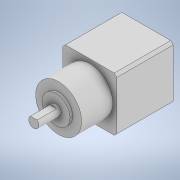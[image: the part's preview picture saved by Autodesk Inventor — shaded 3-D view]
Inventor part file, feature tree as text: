
AUTODESK INVENTOR PART (.ipt)
format: ipt  version: 2021 (Build 250183000, 183)  size: 137,216 bytes
history: native  units: mm
features: extrude x5, sketch x4
ambient origin geometry x8: Origin, YZ Plane, XZ Plane, XY Plane, X Axis, Y Axis, Z Axis, Center Point
bodies: Solid1 (feature_tree)
feature tree (9):
  extrude  "Extrusion1"  Depth=2.0mm
  extrude  "Extrusion2"  Depth=2.0mm
  extrude  "Extrusion3"  Depth=2.0mm
  sketch  "Sketch4"  dims[d6=2.0mm d7=2.0mm d8=42.3mm d9=42.3mm d10=44.2mm d11=0.0mm d12=36.0mm d13=24.5mm d14=0.0mm d15=22.0mm d16=2.0mm d17=0.0mm d18=8.0mm d19=7.0mm d20=17.5mm d21=0.0mm d22=2.3mm d23=0.0mm]
  extrude  "Extrusion4"  Depth=2.0mm
  extrude  "Extrusion5"  Depth=42.3mm
  sketch  "Sketch1"  dims[d0=2.0mm d1=2.0mm]
  sketch  "Sketch2"  dims[d2=2.0mm d3=2.0mm]
  sketch  "Sketch3"  dims[d4=2.0mm d5=2.0mm]
